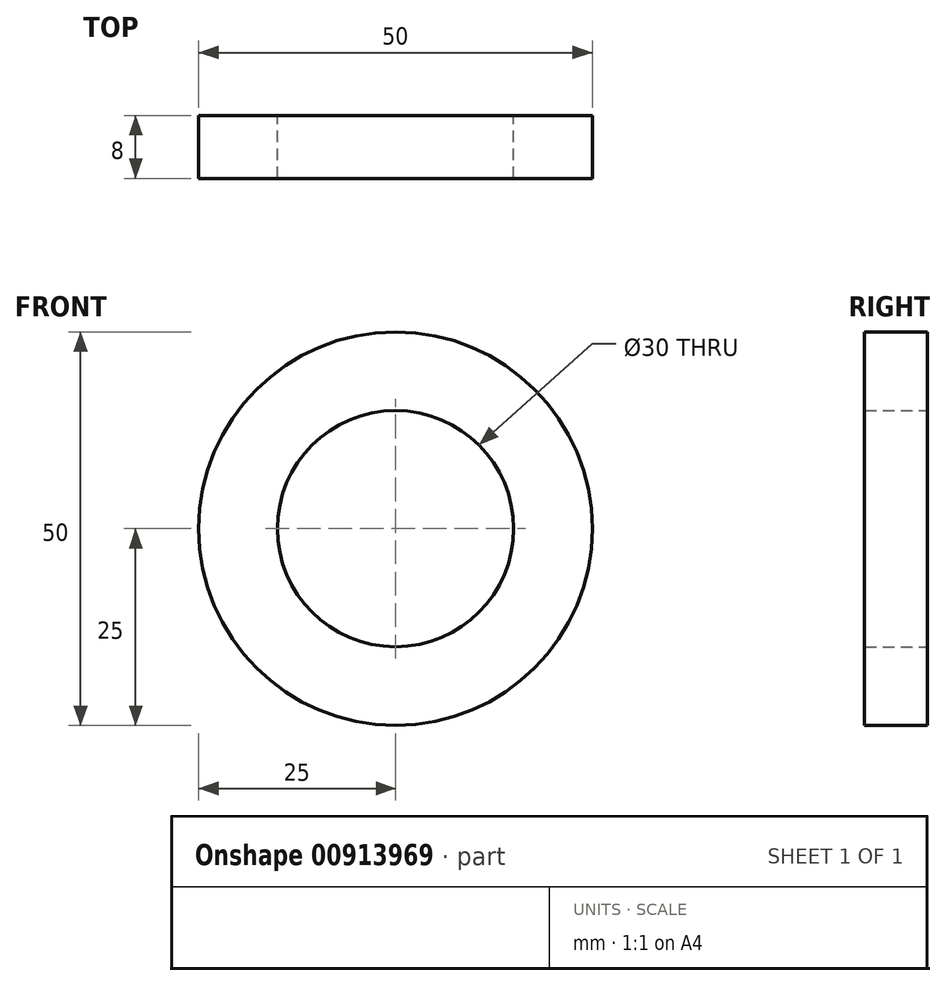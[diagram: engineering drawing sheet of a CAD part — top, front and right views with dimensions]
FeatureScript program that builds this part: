
annotation { "Feature Type Name" : "Feature", "Feature Type Description" : "" }
export const myFeature = defineFeature(function(context is Context, id is Id, definition is map)
    precondition{}
    {
        {
            var Q0;
            Q0=qCreatedBy(makeId("Front.planeOp"),FACE);
            var sketch = newSketch(context, id + "F0", { "sketchPlane" : qUnion([Q0])});
            skCircle(sketch, "E0", {"center": v(-13.07, 39.21) * mm, "radius": 25 * mm});
            skCircle(sketch, "E1", {"center": v(-13.07, 39.21) * mm, "radius": 15 * mm});
            skSolve(sketch);
        }
        {
            var Q0;
            Q0=makeQuery(id+"F0.imprint","IMPRINT",FACE,{"disambiguationData":[TD([[makeQuery(id+"F0.imprint","IMPRINT",EDGE,{"derivedFrom":sQuery(id+"F0.wireOp",EDGE,"E0")}),1.0]])]});
            extrude(context, id + "F1", {"entities" : qUnion([Q0]), "depth" : 8 * mm, "offsetDistance" : 25 * mm});
        }
    });
